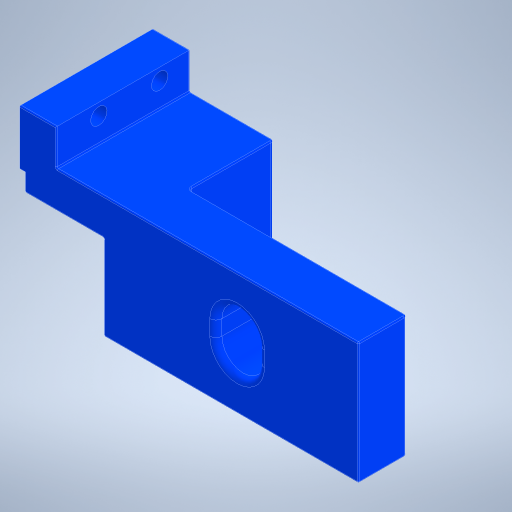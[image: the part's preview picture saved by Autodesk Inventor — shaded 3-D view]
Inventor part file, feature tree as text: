
AUTODESK INVENTOR PART (.ipt)
format: ipt  version: 2023.4 (Build 274418000, 418)  size: 444,416 bytes
history: native  units: in
note: dims shown in document units (in); Inventor stores cm internally (conversion verified against a paired STEP export)
features: sketch x5, extrude x5, other x1, hole x1, fillet x1
ambient origin geometry x8: Origin, YZ Plane, XZ Plane, XY Plane, X Axis, Y Axis, Z Axis, Center Point
bodies: Solid1 (feature_tree)
feature tree (13):
  other  "main_manifold_8v_v02.ipt"
  sketch  "Sketch: reference"  dims[d319=0.3in d1=1.5748in]
  sketch  "Sketch: side profile"  dims[d3=0.3in d5=0.095in]
  sketch  "Sketch: MM holes"  dims[d6=0.3in d7=0.0in]
  extrude  "Ex: MM screws"  TaperAngle=0.0deg  [1 undecoded]
  hole  "Hole: MM screws (4-40)"  [1 undecoded]
  extrude  "Ex: side profile"  Depth=0.3in
  extrude  "Ex: inside face of item post"  Depth=0.2975in
  extrude  "Ex: front face of item post"  Depth=0.04in
  extrude  "Ex: screw hole"  Depth=1.0in TaperAngle=0.0deg
  fillet  "Fillet3"  Radius=0.175in
  sketch  "Sketch:MM: main inlet"  dims[d8=0.135in d9=0.75in d10=0.375in d11=0.25in d12=0.5635in d13=1.0in d14=0.8108in d21=0.2975in d22=0.04in d23=1.0in d24=0.0in d25=0.175in d30=0.05in d34=-0.0674in d43=0.15in d45=0.018in d47=0.89in d48=0.085in d49=0.18in d50=0.04in d51=0.3337in d52=0.15in d56=0.475in d61=0.05in d64=0.41in d65=0.45in d68=0.7in d70=1.5748in d71=0.4in d72=0.0in d73=0.125in d74=0.175in d75=0.0in d76=0.0in d78=0.2in d79=0.01in d82=0.99in d83=0.01in d84=1.0in d86=0.3in d87=1.0in d88=0.0in d89=0.344in d94=120.0deg d95=120.0deg d96=0.25in d98=0.175in d99=0.075in d102=0.1in d105=0.175in d106=0.175in d107=0.1in d108=0.0025in d109=0.025in d110=0.01in d17=0.5in d18=0.0344in d19=0.5in d20=0.0344in d85=0.0in d111=0.0344in]
  sketch  "Sketch:MM: mounting screws:1"  dims[d0=0.3937in d439=0.0in]
note: 2 required parameter values undecoded (feature->parameter linkage not recoverable at this tier; creation-order binding heuristic only, values carry confidence <= 0.55)
